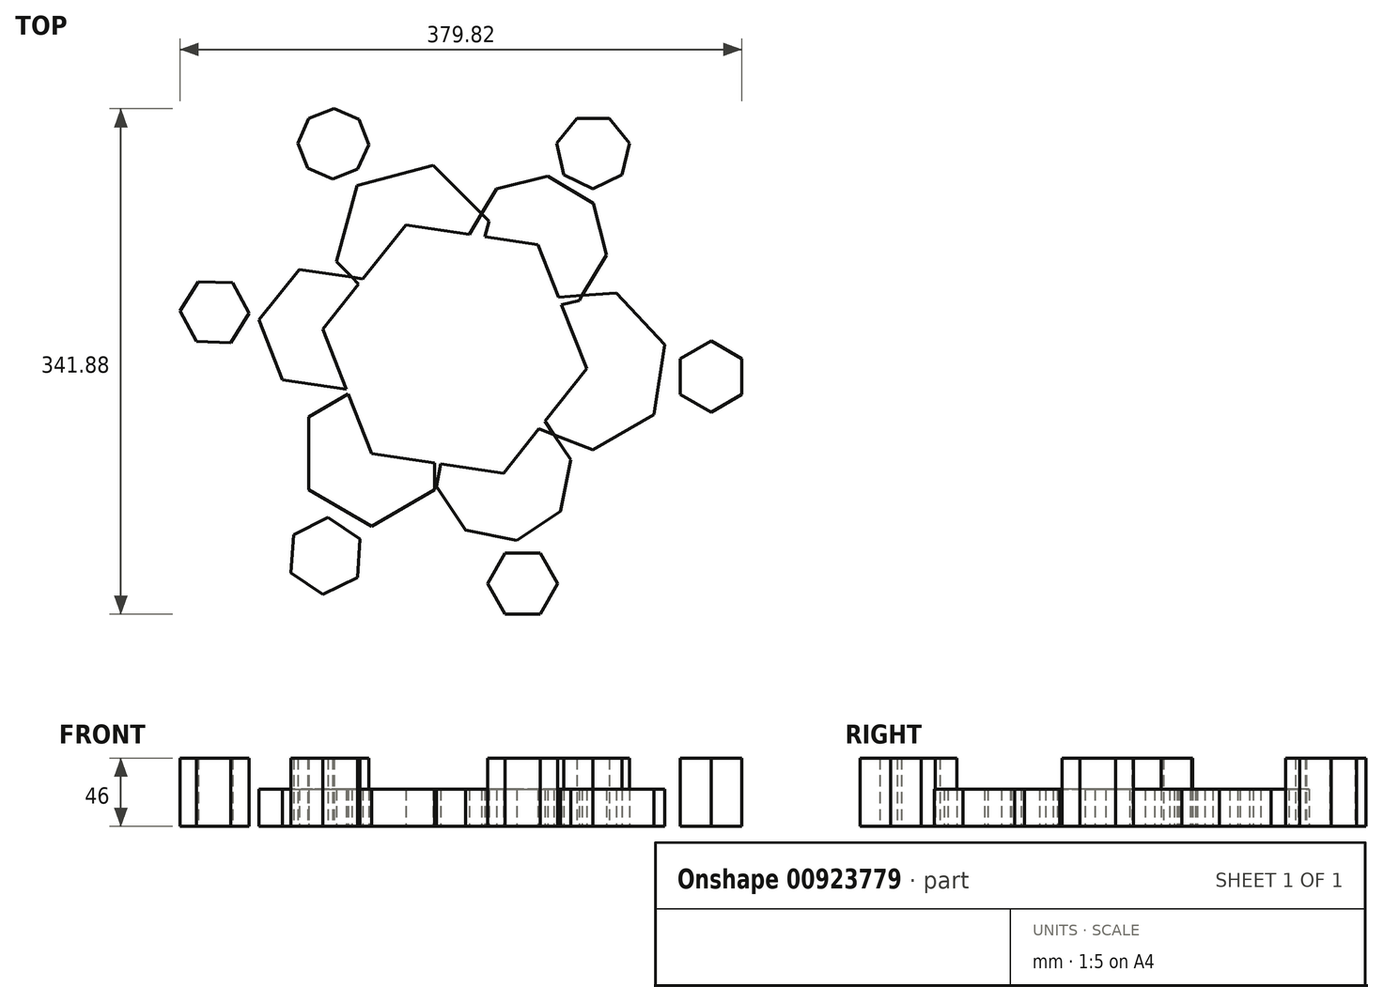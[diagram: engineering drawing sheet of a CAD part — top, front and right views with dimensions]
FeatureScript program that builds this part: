
annotation { "Feature Type Name" : "Feature", "Feature Type Description" : "" }
export const myFeature = defineFeature(function(context is Context, id is Id, definition is map)
    precondition{}
    {
        {
            var Q0;
            Q0=qCreatedBy(makeId("Top.planeOp"),FACE);
            var sketch = newSketch(context, id + "F0", { "sketchPlane" : qUnion([Q0])});
            skLineSegment(sketch, "E0.bottom", {"start": v(182.26, -508.54) * mm, "end": v(289.17, -508.54) * mm});
            skLineSegment(sketch, "E0.top", {"start": v(182.26, -408.52) * mm, "end": v(289.17, -408.52) * mm});
            skLineSegment(sketch, "E0.left", {"start": v(182.26, -508.54) * mm, "end": v(182.26, -408.52) * mm});
            skLineSegment(sketch, "E0.right", {"start": v(289.17, -508.54) * mm, "end": v(289.17, -408.52) * mm});
            skCircle(sketch, "E1.cCircle", {"center": v(235.71, -453.55) * mm, "radius": 78.1 * mm, "construction": true});
            skPoint(sketch, "E1.cCircle.centerSnap0", {"position": v(235.71, -508.54) * mm});
            skLineSegment(sketch, "E1.0", {"start": v(179.55, -524.12) * mm, "end": v(146.52, -440.2) * mm});
            skLineSegment(sketch, "E1.1", {"start": v(146.52, -440.2) * mm, "end": v(202.68, -369.63) * mm});
            skLineSegment(sketch, "E1.2", {"start": v(202.68, -369.63) * mm, "end": v(291.87, -382.98) * mm});
            skLineSegment(sketch, "E1.3", {"start": v(291.87, -382.98) * mm, "end": v(324.9, -466.9) * mm});
            skLineSegment(sketch, "E1.4", {"start": v(324.9, -466.9) * mm, "end": v(268.75, -537.48) * mm});
            skLineSegment(sketch, "E1.5", {"start": v(268.75, -537.48) * mm, "end": v(179.55, -524.12) * mm});
            skPoint(sketch, "E1.0.midPoint", {"position": v(163.03, -482.16) * mm});
            skCircle(sketch, "E2.cCircle", {"center": v(207.32, -380.79) * mm, "radius": 46.23 * mm, "construction": true});
            skLineSegment(sketch, "E2.0", {"start": v(244.99, -418.62) * mm, "end": v(193.4, -432.32) * mm});
            skLineSegment(sketch, "E2.1", {"start": v(193.4, -432.32) * mm, "end": v(155.73, -394.5) * mm});
            skLineSegment(sketch, "E2.2", {"start": v(155.73, -394.5) * mm, "end": v(169.65, -342.96) * mm});
            skLineSegment(sketch, "E2.3", {"start": v(169.65, -342.96) * mm, "end": v(221.24, -329.25) * mm});
            skLineSegment(sketch, "E2.4", {"start": v(221.24, -329.25) * mm, "end": v(258.91, -367.08) * mm});
            skLineSegment(sketch, "E2.5", {"start": v(258.91, -367.08) * mm, "end": v(244.99, -418.62) * mm});
            skPoint(sketch, "E2.0.midPoint", {"position": v(219.2, -425.47) * mm});
            skCircle(sketch, "E3.cCircle", {"center": v(146.52, -440.2) * mm, "radius": 37.7 * mm, "construction": true});
            skLineSegment(sketch, "E3.0", {"start": v(119.4, -474.26) * mm, "end": v(103.47, -433.76) * mm});
            skLineSegment(sketch, "E3.1", {"start": v(103.47, -433.76) * mm, "end": v(130.57, -399.7) * mm});
            skLineSegment(sketch, "E3.2", {"start": v(130.57, -399.7) * mm, "end": v(173.62, -406.14) * mm});
            skLineSegment(sketch, "E3.3", {"start": v(173.62, -406.14) * mm, "end": v(189.56, -446.65) * mm});
            skLineSegment(sketch, "E3.4", {"start": v(189.56, -446.65) * mm, "end": v(162.46, -480.7) * mm});
            skLineSegment(sketch, "E3.5", {"start": v(162.46, -480.7) * mm, "end": v(119.4, -474.26) * mm});
            skPoint(sketch, "E3.0.midPoint", {"position": v(111.44, -454) * mm});
            skCircle(sketch, "E4.cCircle", {"center": v(268.75, -537.48) * mm, "radius": 42.75 * mm, "construction": true});
            skLineSegment(sketch, "E4.0", {"start": v(307.2, -563.22) * mm, "end": v(277.74, -582.87) * mm});
            skLineSegment(sketch, "E4.1", {"start": v(277.74, -582.87) * mm, "end": v(243, -575.93) * mm});
            skLineSegment(sketch, "E4.2", {"start": v(243, -575.93) * mm, "end": v(223.35, -546.47) * mm});
            skLineSegment(sketch, "E4.3", {"start": v(223.35, -546.47) * mm, "end": v(230.3, -511.74) * mm});
            skLineSegment(sketch, "E4.4", {"start": v(230.3, -511.74) * mm, "end": v(259.75, -492.08) * mm});
            skLineSegment(sketch, "E4.5", {"start": v(259.75, -492.08) * mm, "end": v(294.49, -499.02) * mm});
            skLineSegment(sketch, "E4.6", {"start": v(294.49, -499.02) * mm, "end": v(314.14, -528.48) * mm});
            skLineSegment(sketch, "E4.7", {"start": v(314.14, -528.48) * mm, "end": v(307.2, -563.22) * mm});
            skPoint(sketch, "E4.0.midPoint", {"position": v(292.47, -573.04) * mm});
            skCircle(sketch, "E5.cCircle", {"center": v(324.9, -466.9) * mm, "radius": 49.67 * mm, "construction": true});
            skLineSegment(sketch, "E5.0", {"start": v(377.57, -450.6) * mm, "end": v(370.5, -497.92) * mm});
            skLineSegment(sketch, "E5.1", {"start": v(370.5, -497.92) * mm, "end": v(329.08, -521.88) * mm});
            skLineSegment(sketch, "E5.2", {"start": v(329.08, -521.88) * mm, "end": v(284.53, -504.44) * mm});
            skLineSegment(sketch, "E5.3", {"start": v(284.53, -504.44) * mm, "end": v(270.39, -458.74) * mm});
            skLineSegment(sketch, "E5.4", {"start": v(270.39, -458.74) * mm, "end": v(297.3, -419.19) * mm});
            skLineSegment(sketch, "E5.5", {"start": v(297.3, -419.19) * mm, "end": v(345, -415.57) * mm});
            skLineSegment(sketch, "E5.6", {"start": v(345, -415.57) * mm, "end": v(377.57, -450.6) * mm});
            skPoint(sketch, "E5.0.midPoint", {"position": v(374.03, -474.26) * mm});
            skCircle(sketch, "E6.cCircle", {"center": v(291.87, -382.98) * mm, "radius": 43.29 * mm, "construction": true});
            skLineSegment(sketch, "E6.0", {"start": v(298.76, -336.64) * mm, "end": v(329.52, -355.08) * mm});
            skLineSegment(sketch, "E6.1", {"start": v(329.52, -355.08) * mm, "end": v(338.22, -389.87) * mm});
            skLineSegment(sketch, "E6.2", {"start": v(338.22, -389.87) * mm, "end": v(319.78, -420.63) * mm});
            skLineSegment(sketch, "E6.3", {"start": v(319.78, -420.63) * mm, "end": v(284.99, -429.33) * mm});
            skLineSegment(sketch, "E6.4", {"start": v(284.99, -429.33) * mm, "end": v(254.23, -410.88) * mm});
            skLineSegment(sketch, "E6.5", {"start": v(254.23, -410.88) * mm, "end": v(245.53, -376.1) * mm});
            skLineSegment(sketch, "E6.6", {"start": v(245.53, -376.1) * mm, "end": v(263.97, -345.34) * mm});
            skLineSegment(sketch, "E6.7", {"start": v(263.97, -345.34) * mm, "end": v(298.76, -336.64) * mm});
            skPoint(sketch, "E6.0.midPoint", {"position": v(314.14, -345.86) * mm});
            skPoint(sketch, "E7.cCircle.perimeterSnap0", {"position": v(140.93, -477.48) * mm});
            skPoint(sketch, "E7.0.midPoint.positionSnap0", {"position": v(140.93, -477.48) * mm});
            skCircle(sketch, "E8.cCircle", {"center": v(235.71, -453.55) * mm, "radius": 34.95 * mm, "construction": true});
            skLineSegment(sketch, "E8.0", {"start": v(214.17, -491) * mm, "end": v(193.45, -444.64) * mm});
            skLineSegment(sketch, "E8.1", {"start": v(193.45, -444.64) * mm, "end": v(231.13, -410.6) * mm});
            skLineSegment(sketch, "E8.2", {"start": v(231.13, -410.6) * mm, "end": v(275.15, -435.92) * mm});
            skLineSegment(sketch, "E8.3", {"start": v(275.15, -435.92) * mm, "end": v(264.67, -485.6) * mm});
            skLineSegment(sketch, "E8.4", {"start": v(264.67, -485.6) * mm, "end": v(214.17, -491) * mm});
            skPoint(sketch, "E8.0.midPoint", {"position": v(203.81, -467.82) * mm});
            skCircle(sketch, "E9.cCircle", {"center": v(179.55, -524.12) * mm, "radius": 42.64 * mm, "construction": true});
            skLineSegment(sketch, "E9.0", {"start": v(136.91, -548.74) * mm, "end": v(136.91, -499.5) * mm});
            skLineSegment(sketch, "E9.1", {"start": v(136.91, -499.5) * mm, "end": v(179.55, -474.9) * mm});
            skLineSegment(sketch, "E9.2", {"start": v(179.55, -474.9) * mm, "end": v(222.19, -499.5) * mm});
            skLineSegment(sketch, "E9.3", {"start": v(222.19, -499.5) * mm, "end": v(222.19, -548.74) * mm});
            skLineSegment(sketch, "E9.4", {"start": v(222.19, -548.74) * mm, "end": v(179.55, -573.36) * mm});
            skLineSegment(sketch, "E9.5", {"start": v(179.55, -573.36) * mm, "end": v(136.91, -548.74) * mm});
            skPoint(sketch, "E9.0.midPoint", {"position": v(136.91, -524.12) * mm});
            skSolve(sketch);
        }
        {
            var Q0;
            {var subQ0=sQuery(id+"F0.wireOp",EDGE,"E9.0");Q0=makeQuery(id+"F0.imprint","IMPRINT",FACE,{"disambiguationData":[TD([[makeQuery(id+"F0.imprint","IMPRINT",EDGE,{"derivedFrom":subQ0}),-1.0]])]});}
            var Q1;
            Q1=makeQuery(id+"F0.imprint","IMPRINT",FACE,{"disambiguationData":[TD([[makeQuery(id+"F0.imprint","IMPRINT",EDGE,{"derivedFrom":sQuery(id+"F0.wireOp",EDGE,"E3.0")}),-1.0]])]});
            var Q2;
            {var subQ0=sQuery(id+"F0.wireOp",EDGE,"E2.2");Q2=makeQuery(id+"F0.imprint","IMPRINT",FACE,{"disambiguationData":[TD([[makeQuery(id+"F0.imprint","IMPRINT",EDGE,{"derivedFrom":subQ0}),-1.0]])]});}
            var Q3;
            Q3=makeQuery(id+"F0.imprint","IMPRINT",FACE,{"disambiguationData":[TD([[makeQuery(id+"F0.imprint","IMPRINT",EDGE,{"derivedFrom":sQuery(id+"F0.wireOp",EDGE,"E6.0")}),-1.0]])]});
            var Q4;
            Q4=makeQuery(id+"F0.imprint","IMPRINT",FACE,{"disambiguationData":[TD([[makeQuery(id+"F0.imprint","IMPRINT",EDGE,{"derivedFrom":sQuery(id+"F0.wireOp",EDGE,"E5.0")}),-1.0]])]});
            var Q5;
            Q5=makeQuery(id+"F0.imprint","IMPRINT",FACE,{"disambiguationData":[TD([[makeQuery(id+"F0.imprint","IMPRINT",EDGE,{"derivedFrom":sQuery(id+"F0.wireOp",EDGE,"E4.0")}),-1.0]])]});
            extrude(context, id + "F1", {"entities" : qUnion([Q0, Q1, Q2, Q3, Q4, Q5]), "depth" : 25 * mm, "offsetDistance" : 25 * mm});
        }
        {
            var Q0;
            Q0=qCreatedBy(makeId("Top.planeOp"),FACE);
            var sketch = newSketch(context, id + "F2", { "sketchPlane" : qUnion([Q0])});
            skCircle(sketch, "E10", {"center": v(101.07, -431.74) * mm, "radius": 34.42 * mm});
            skCircle(sketch, "E11", {"center": v(167.76, -341.25) * mm, "radius": 32.66 * mm});
            skCircle(sketch, "E12", {"center": v(315.18, -350.08) * mm, "radius": 34.05 * mm});
            skCircle(sketch, "E13", {"center": v(372.53, -470.52) * mm, "radius": 39.55 * mm});
            skCircle(sketch, "E14", {"center": v(277.11, -581.56) * mm, "radius": 31.56 * mm});
            skCircle(sketch, "E15", {"center": v(164.69, -563.23) * mm, "radius": 33 * mm});
            skLineSegment(sketch, "E16", {"start": v(277.11, -581.56) * mm, "end": v(230.02, -643.89) * mm});
            skLineSegment(sketch, "E17", {"start": v(230.02, -643.89) * mm, "end": v(164.69, -563.23) * mm});
            skLineSegment(sketch, "E18", {"start": v(164.69, -563.23) * mm, "end": v(78.9, -547.77) * mm});
            skLineSegment(sketch, "E19", {"start": v(78.9, -547.77) * mm, "end": v(101.07, -431.74) * mm});
            skLineSegment(sketch, "E20", {"start": v(101.07, -431.74) * mm, "end": v(78.9, -333.88) * mm});
            skLineSegment(sketch, "E21", {"start": v(78.9, -333.88) * mm, "end": v(167.76, -341.25) * mm});
            skLineSegment(sketch, "E22", {"start": v(167.76, -341.25) * mm, "end": v(239.67, -250.28) * mm});
            skLineSegment(sketch, "E23", {"start": v(239.67, -250.28) * mm, "end": v(315.18, -350.08) * mm});
            skLineSegment(sketch, "E24", {"start": v(315.18, -350.08) * mm, "end": v(426.85, -360.03) * mm});
            skLineSegment(sketch, "E25", {"start": v(426.85, -360.03) * mm, "end": v(372.53, -470.52) * mm});
            skLineSegment(sketch, "E26", {"start": v(372.53, -470.52) * mm, "end": v(411.99, -591.52) * mm});
            skLineSegment(sketch, "E27", {"start": v(411.99, -591.52) * mm, "end": v(277.11, -581.56) * mm});
            skCircle(sketch, "E28", {"center": v(78.9, -333.88) * mm, "radius": 40.9 * mm});
            skCircle(sketch, "E29", {"center": v(239.67, -250.28) * mm, "radius": 54.64 * mm});
            skCircle(sketch, "E30", {"center": v(426.85, -360.03) * mm, "radius": 46.48 * mm});
            skCircle(sketch, "E31", {"center": v(411.99, -591.52) * mm, "radius": 46.23 * mm});
            skCircle(sketch, "E32", {"center": v(230.02, -643.89) * mm, "radius": 40.44 * mm});
            skCircle(sketch, "E33", {"center": v(78.9, -547.77) * mm, "radius": 58.37 * mm});
            skSolve(sketch);
        }
        {
            var Q0;
            Q0=sQuery(id+"F2.wireOp",EDGE,"E14");
            var Q1;
            Q1=sQuery(id+"F2.wireOp",EDGE,"E15");
            var Q2;
            Q2=sQuery(id+"F2.wireOp",EDGE,"E10");
            var Q3;
            Q3=sQuery(id+"F2.wireOp",EDGE,"E11");
            var Q4;
            Q4=sQuery(id+"F2.wireOp",EDGE,"E12");
            var Q5;
            Q5=sQuery(id+"F2.wireOp",EDGE,"E13");
            extrude(context, id + "F3", {"bodyType" : ToolBodyType.SURFACE, "surfaceEntities" : qUnion([Q0, Q1, Q2, Q3, Q4, Q5]), "depth" : 25 * mm, "offsetDistance" : 25 * mm});
        }
        {
            var Q0;
            Q0=qCreatedBy(makeId("Top.planeOp"),FACE);
            var sketch = newSketch(context, id + "F4", { "sketchPlane" : qUnion([Q0])});
            skCircle(sketch, "E34.cCircle", {"center": v(73.35, -428.62) * mm, "radius": 20.2 * mm, "construction": true});
            skLineSegment(sketch, "E34.0", {"start": v(61.05, -448.44) * mm, "end": v(50.04, -427.87) * mm});
            skLineSegment(sketch, "E34.1", {"start": v(50.04, -427.87) * mm, "end": v(62.34, -408.05) * mm});
            skLineSegment(sketch, "E34.2", {"start": v(62.34, -408.05) * mm, "end": v(85.66, -408.8) * mm});
            skLineSegment(sketch, "E34.3", {"start": v(85.66, -408.8) * mm, "end": v(96.67, -429.36) * mm});
            skLineSegment(sketch, "E34.4", {"start": v(96.67, -429.36) * mm, "end": v(84.37, -449.18) * mm});
            skLineSegment(sketch, "E34.5", {"start": v(84.37, -449.18) * mm, "end": v(61.05, -448.44) * mm});
            skPoint(sketch, "E34.0.midPoint", {"position": v(55.54, -438.16) * mm});
            skCircle(sketch, "E35.cCircle", {"center": v(148.4, -593.5) * mm, "radius": 22.55 * mm, "construction": true});
            skLineSegment(sketch, "E35.0", {"start": v(146.7, -619.48) * mm, "end": v(125.05, -605.03) * mm});
            skLineSegment(sketch, "E35.1", {"start": v(125.05, -605.03) * mm, "end": v(126.73, -579.05) * mm});
            skLineSegment(sketch, "E35.2", {"start": v(126.73, -579.05) * mm, "end": v(150.08, -567.52) * mm});
            skLineSegment(sketch, "E35.3", {"start": v(150.08, -567.52) * mm, "end": v(171.74, -581.97) * mm});
            skLineSegment(sketch, "E35.4", {"start": v(171.74, -581.97) * mm, "end": v(170.05, -607.96) * mm});
            skLineSegment(sketch, "E35.5", {"start": v(170.05, -607.96) * mm, "end": v(146.7, -619.48) * mm});
            skPoint(sketch, "E35.0.midPoint", {"position": v(135.87, -612.26) * mm});
            skArc(sketch, "E36.cCircle", {"start": v(263.88, -601.97) * mm, "mid": v(291.98, -630.07) * mm, "end": v(281.7, -591.68) * mm, "construction": true});
            skLineSegment(sketch, "E36.0", {"start": v(293.57, -632.83) * mm, "end": v(269.82, -632.83) * mm});
            skLineSegment(sketch, "E36.1", {"start": v(269.82, -632.83) * mm, "end": v(257.94, -612.26) * mm});
            skLineSegment(sketch, "E36.2", {"start": v(257.94, -612.26) * mm, "end": v(269.82, -591.68) * mm});
            skLineSegment(sketch, "E36.3", {"start": v(269.82, -591.68) * mm, "end": v(293.57, -591.68) * mm});
            skLineSegment(sketch, "E36.4", {"start": v(293.57, -591.68) * mm, "end": v(305.45, -612.26) * mm});
            skLineSegment(sketch, "E36.5", {"start": v(305.45, -612.26) * mm, "end": v(293.57, -632.83) * mm});
            skPoint(sketch, "E36.0.midPoint", {"position": v(281.7, -632.83) * mm});
            skCircle(sketch, "E37.cCircle", {"center": v(409.02, -472.22) * mm, "radius": 20.84 * mm, "construction": true});
            skLineSegment(sketch, "E37.0", {"start": v(429.86, -460.19) * mm, "end": v(429.86, -484.25) * mm});
            skLineSegment(sketch, "E37.1", {"start": v(429.86, -484.25) * mm, "end": v(409.02, -496.29) * mm});
            skLineSegment(sketch, "E37.2", {"start": v(409.02, -496.29) * mm, "end": v(388.18, -484.25) * mm});
            skLineSegment(sketch, "E37.3", {"start": v(388.18, -484.25) * mm, "end": v(388.18, -460.19) * mm});
            skLineSegment(sketch, "E37.4", {"start": v(388.18, -460.19) * mm, "end": v(409.02, -448.15) * mm});
            skLineSegment(sketch, "E37.5", {"start": v(409.02, -448.15) * mm, "end": v(429.86, -460.19) * mm});
            skPoint(sketch, "E37.0.midPoint", {"position": v(429.86, -472.22) * mm});
            skCircle(sketch, "E38.cCircle", {"center": v(329.24, -320.1) * mm, "radius": 22.69 * mm, "construction": true});
            skLineSegment(sketch, "E38.0", {"start": v(318.31, -297.41) * mm, "end": v(340.16, -297.41) * mm});
            skLineSegment(sketch, "E38.1", {"start": v(340.16, -297.41) * mm, "end": v(353.79, -314.5) * mm});
            skLineSegment(sketch, "E38.2", {"start": v(353.79, -314.5) * mm, "end": v(348.93, -335.8) * mm});
            skLineSegment(sketch, "E38.3", {"start": v(348.93, -335.8) * mm, "end": v(329.24, -345.28) * mm});
            skLineSegment(sketch, "E38.4", {"start": v(329.24, -345.28) * mm, "end": v(309.55, -335.8) * mm});
            skLineSegment(sketch, "E38.5", {"start": v(309.55, -335.8) * mm, "end": v(304.69, -314.5) * mm});
            skLineSegment(sketch, "E38.6", {"start": v(304.69, -314.5) * mm, "end": v(318.31, -297.41) * mm});
            skPoint(sketch, "E38.0.midPoint", {"position": v(329.24, -297.41) * mm});
            skCircle(sketch, "E39.cCircle", {"center": v(153.69, -314.8) * mm, "radius": 22.04 * mm, "construction": true});
            skPoint(sketch, "E39.cCircle.perimeterSnap0", {"position": v(311.5, -305.95) * mm});
            skLineSegment(sketch, "E39.0", {"start": v(129.84, -314.31) * mm, "end": v(137.17, -297.6) * mm});
            skLineSegment(sketch, "E39.1", {"start": v(137.17, -297.6) * mm, "end": v(154.17, -290.95) * mm});
            skLineSegment(sketch, "E39.2", {"start": v(154.17, -290.95) * mm, "end": v(170.9, -298.28) * mm});
            skLineSegment(sketch, "E39.3", {"start": v(170.9, -298.28) * mm, "end": v(177.54, -315.28) * mm});
            skLineSegment(sketch, "E39.4", {"start": v(177.54, -315.28) * mm, "end": v(170.21, -332) * mm});
            skLineSegment(sketch, "E39.5", {"start": v(170.21, -332) * mm, "end": v(153.2, -338.65) * mm});
            skLineSegment(sketch, "E39.6", {"start": v(153.2, -338.65) * mm, "end": v(136.48, -331.32) * mm});
            skLineSegment(sketch, "E39.7", {"start": v(136.48, -331.32) * mm, "end": v(129.84, -314.31) * mm});
            skPoint(sketch, "E39.0.midPoint", {"position": v(133.5, -305.95) * mm});
            skPoint(sketch, "E39.0.midPoint.positionSnap0", {"position": v(311.5, -305.95) * mm});
            skSolve(sketch);
        }
        {
            var Q0;
            Q0=makeQuery(id+"F4.imprint","IMPRINT",FACE,{"disambiguationData":[TD([[makeQuery(id+"F4.imprint","IMPRINT",EDGE,{"derivedFrom":sQuery(id+"F4.wireOp",EDGE,"E34.0")}),-1.0]])]});
            var Q1;
            Q1=makeQuery(id+"F4.imprint","IMPRINT",FACE,{"disambiguationData":[TD([[makeQuery(id+"F4.imprint","IMPRINT",EDGE,{"derivedFrom":sQuery(id+"F4.wireOp",EDGE,"E39.0")}),-1.0]])]});
            var Q2;
            Q2=makeQuery(id+"F4.imprint","IMPRINT",FACE,{"disambiguationData":[TD([[makeQuery(id+"F4.imprint","IMPRINT",EDGE,{"derivedFrom":sQuery(id+"F4.wireOp",EDGE,"E37.0")}),-1.0]])]});
            var Q3;
            Q3=makeQuery(id+"F4.imprint","IMPRINT",FACE,{"disambiguationData":[TD([[makeQuery(id+"F4.imprint","IMPRINT",EDGE,{"derivedFrom":sQuery(id+"F4.wireOp",EDGE,"E36.0")}),-1.0]])]});
            var Q4;
            Q4=makeQuery(id+"F4.imprint","IMPRINT",FACE,{"disambiguationData":[TD([[makeQuery(id+"F4.imprint","IMPRINT",EDGE,{"derivedFrom":sQuery(id+"F4.wireOp",EDGE,"E35.0")}),-1.0]])]});
            var Q5;
            Q5=makeQuery(id+"F4.imprint","IMPRINT",FACE,{"disambiguationData":[TD([[makeQuery(id+"F4.imprint","IMPRINT",EDGE,{"derivedFrom":sQuery(id+"F4.wireOp",EDGE,"E38.0")}),-1.0]])]});
            extrude(context, id + "F5", {"entities" : qUnion([Q0, Q1, Q2, Q3, Q4, Q5]), "depth" : 46 * mm, "offsetDistance" : 25 * mm});
        }
    });
